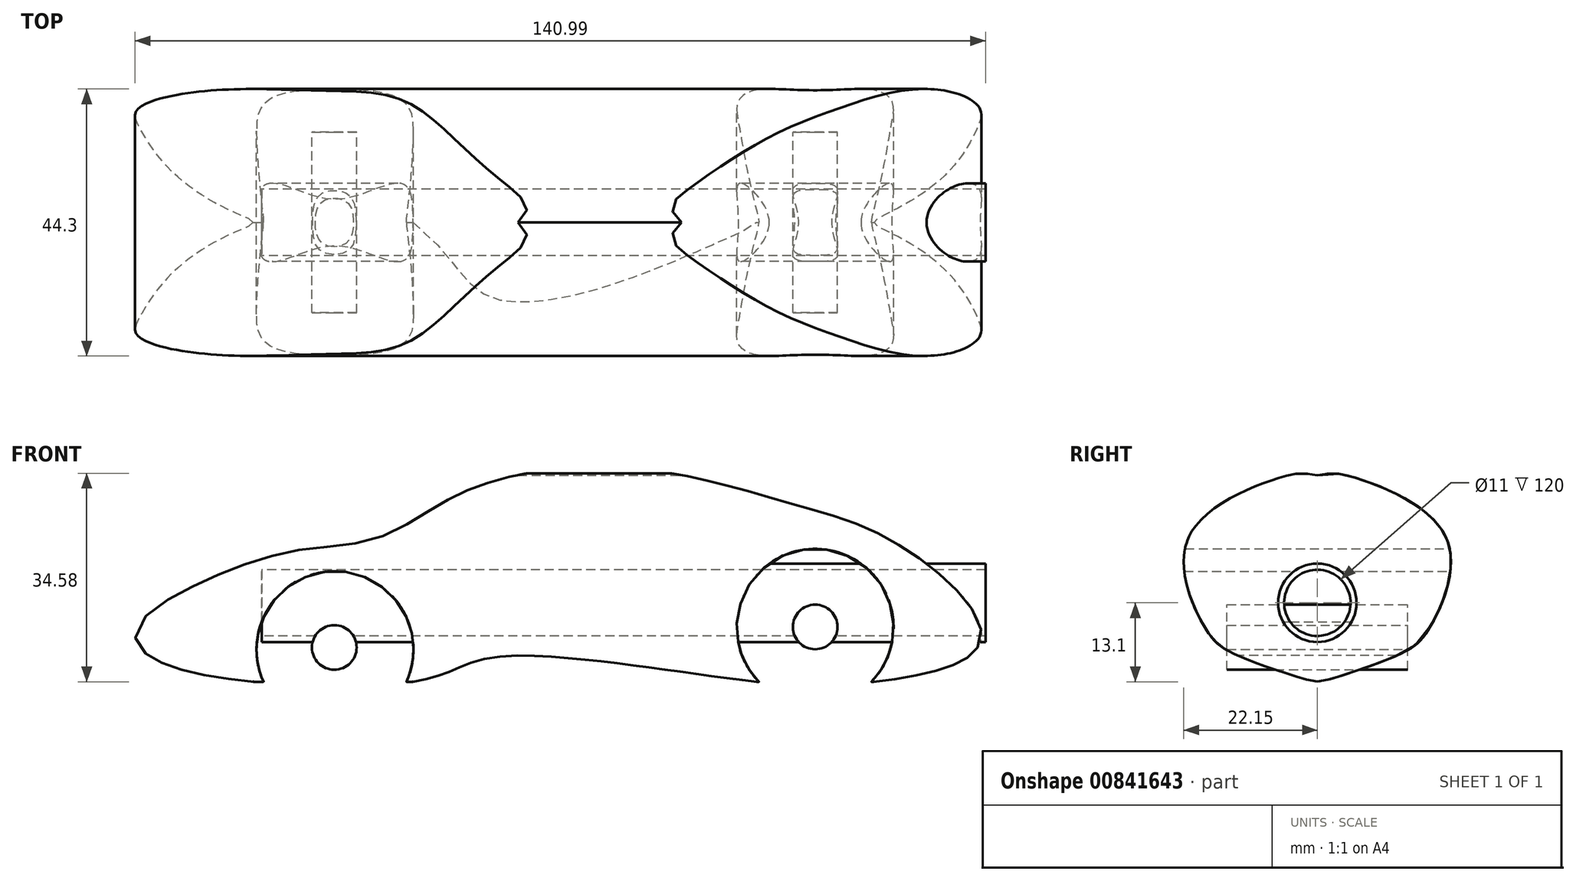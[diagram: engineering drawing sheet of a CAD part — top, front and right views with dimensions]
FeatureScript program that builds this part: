
annotation { "Feature Type Name" : "Feature", "Feature Type Description" : "" }
export const myFeature = defineFeature(function(context is Context, id is Id, definition is map)
    precondition{}
    {
        {
            var Q0;
            Q0=qCreatedBy(makeId("Front.planeOp"),FACE);
            var sketch = newSketch(context, id + "F0", { "sketchPlane" : qUnion([Q0])});
            skFitSpline(sketch, "E0", {"points": [v(-59.64, -4.2) * mm, v(-80.93, 4.21) * mm, v(-71.03, 11.94) * mm, v(-54.11, 17.74) * mm, v(-40.35, 19.91) * mm, v(-26.58, 27.4) * mm, v(-6.04, 31.51) * mm, v(11.6, 29.82) * mm, v(28.75, 25.23) * mm, v(44.36, 19.4) * mm, v(58.84, 6) * mm, v(41.05, -4.1) * mm], "startDerivative": vector(-453.54, 31.44) * mm, "endDerivative": vector(-506.77, -53.77) * mm});
            skArc(sketch, "E1", {"start": v(-36.05, -4.2) * mm, "mid": v(-47.84, 14.28) * mm, "end": v(-59.64, -4.2) * mm});
            skArc(sketch, "E2", {"start": v(41.05, -4.1) * mm, "mid": v(31.77, 18) * mm, "end": v(22.48, -4.1) * mm});
            skFitSpline(sketch, "E3", {"points": [v(-36.05, -4.2) * mm, v(-21.55, 0) * mm, v(22.48, -4.1) * mm], "startDerivative": vector(59.58, 6.01) * mm, "endDerivative": vector(57.48, -5.89) * mm});
            skLineSegment(sketch, "E4", {"start": v(-36.05, -4.2) * mm, "end": v(22.48, -4.1) * mm});
            skSolve(sketch);
        }
        {
            var Q0;
            Q0=makeQuery(id+"F0.imprint","IMPRINT",FACE,{"disambiguationData":[TD([[makeQuery(id+"F0.imprint","IMPRINT",EDGE,{"derivedFrom":sQuery(id+"F0.wireOp",EDGE,"E0")}),-1.0]])]});
            extrude(context, id + "F1", {"entities" : qUnion([Q0]), "endBound" : BoundingType.SYMMETRIC, "depth" : 45 * mm, "offsetDistance" : 25 * mm});
        }
        {
            var Q0;
            Q0=qCreatedBy(makeId("Right.planeOp"),FACE);
            var sketch = newSketch(context, id + "F2", { "sketchPlane" : qUnion([Q0])});
            skFitSpline(sketch, "E5", {"points": [v(0, 30.22) * mm, v(3.28, 30.45) * mm, v(6.23, 29.8) * mm, v(21.23, 20.11) * mm, v(18.59, 4.84) * mm, v(12.58, 0) * mm, v(0, -4.05) * mm, v(0, -3.93) * mm], "startDerivative": vector(56.54, 11.22) * mm, "endDerivative": vector(3.77, 8.29) * mm});
            skFitSpline(sketch, "E6.MirrorCS", {"points": [v(0, 30.22) * mm, v(-3.28, 30.45) * mm, v(-6.23, 29.8) * mm, v(-21.23, 20.11) * mm, v(-18.59, 4.84) * mm, v(-12.58, 0) * mm, v(0, -4.05) * mm, v(0, -3.93) * mm], "startDerivative": vector(-56.54, 11.22) * mm, "endDerivative": vector(-3.77, 8.29) * mm});
            skLineSegment(sketch, "E7.bottom", {"start": v(36.38, 39.95) * mm, "end": v(-33.23, 39.95) * mm});
            skLineSegment(sketch, "E7.top", {"start": v(36.38, -10.43) * mm, "end": v(-33.23, -10.43) * mm});
            skLineSegment(sketch, "E7.left", {"start": v(36.38, 39.95) * mm, "end": v(36.38, -10.43) * mm});
            skLineSegment(sketch, "E7.right", {"start": v(-33.23, 39.95) * mm, "end": v(-33.23, -10.43) * mm});
            skSolve(sketch);
        }
        {
            var Q0;
            Q0=makeQuery(id+"F2.imprint","IMPRINT",FACE,{"disambiguationData":[TD([[makeQuery(id+"F2.imprint","IMPRINT",EDGE,{"derivedFrom":sQuery(id+"F2.wireOp",EDGE,"E7.bottom")}),1.0]])]});
            extrude(context, id + "F3", {"entities" : qUnion([Q0]), "operationType" : NewBodyOperationType.REMOVE, "endBound" : BoundingType.SYMMETRIC, "oppositeDirection" : true, "depth" : 170 * mm, "offsetDistance" : 25 * mm});
        }
        {
            var Q0;
            Q0=makeQuery(id+"F2.imprint","IMPRINT",FACE,{"disambiguationData":[TD([[makeQuery(id+"F2.imprint","IMPRINT",EDGE,{"derivedFrom":sQuery(id+"F2.wireOp",EDGE,"E7.bottom")}),1.0]])]});
            var sketch = newSketch(context, id + "F4", { "sketchPlane" : qUnion([Q0])});
            skCircle(sketch, "E8", {"center": v(0, 9.03) * mm, "radius": 6.5 * mm});
            skCircle(sketch, "E9", {"center": v(0, 9.03) * mm, "radius": 5.5 * mm});
            skSolve(sketch);
        }
        {
            var Q0;
            Q0=makeQuery(id+"F4.imprint","IMPRINT",FACE,{"disambiguationData":[TD([[makeQuery(id+"F4.imprint","IMPRINT",EDGE,{"derivedFrom":sQuery(id+"F4.wireOp",EDGE,"E9")}),1.0]])]});
            var Q1;
            Q1=sQuery(id+"F4.wireOp",EDGE,"E8");
            extrude(context, id + "F5", {"entities" : qUnion([Q0]), "operationType" : NewBodyOperationType.REMOVE, "surfaceEntities" : qUnion([Q1]), "depth" : 60 * mm, "offsetDistance" : 25 * mm, "hasSecondDirection" : true, "secondDirectionOppositeDirection" : true, "secondDirectionDepth" : 60 * mm});
        }
        {
            var Q0;
            Q0=makeQuery(id+"F4.imprint","IMPRINT",FACE,{"disambiguationData":[TD([[makeQuery(id+"F4.imprint","IMPRINT",EDGE,{"derivedFrom":sQuery(id+"F4.wireOp",EDGE,"E8")}),1.0]])]});
            extrude(context, id + "F6", {"entities" : qUnion([Q0]), "operationType" : NewBodyOperationType.ADD, "depth" : 60 * mm, "offsetDistance" : 25 * mm, "hasSecondDirection" : true, "secondDirectionOppositeDirection" : true, "secondDirectionDepth" : 60 * mm});
        }
        {
            var Q0;
            Q0=qCreatedBy(makeId("Front.planeOp"),FACE);
            var sketch = newSketch(context, id + "F7", { "sketchPlane" : qUnion([Q0])});
            skCircle(sketch, "E10", {"center": v(-47.95, 1.63) * mm, "radius": 3.7 * mm});
            skSolve(sketch);
        }
        {
            var Q0;
            Q0=makeQuery(id+"F7.imprint","IMPRINT",FACE,{"disambiguationData":[TD([[makeQuery(id+"F7.imprint","IMPRINT",EDGE,{"derivedFrom":sQuery(id+"F7.wireOp",EDGE,"E10")}),1.0]])]});
            extrude(context, id + "F8", {"entities" : qUnion([Q0]), "operationType" : NewBodyOperationType.ADD, "depth" : 15 * mm, "offsetDistance" : 25 * mm, "hasSecondDirection" : true, "secondDirectionOppositeDirection" : true, "secondDirectionDepth" : 15 * mm});
        }
        {
            var Q0;
            Q0=qCreatedBy(makeId("Front.planeOp"),FACE);
            var sketch = newSketch(context, id + "F9", { "sketchPlane" : qUnion([Q0])});
            skCircle(sketch, "E11", {"center": v(31.77, 5.02) * mm, "radius": 3.7 * mm});
            skSolve(sketch);
        }
        {
            var Q0;
            Q0=makeQuery(id+"F9.imprint","IMPRINT",FACE,{"disambiguationData":[TD([[makeQuery(id+"F9.imprint","IMPRINT",EDGE,{"derivedFrom":sQuery(id+"F9.wireOp",EDGE,"E11")}),1.0]])]});
            extrude(context, id + "F10", {"entities" : qUnion([Q0]), "operationType" : NewBodyOperationType.ADD, "depth" : 15 * mm, "offsetDistance" : 25 * mm, "hasSecondDirection" : true, "secondDirectionOppositeDirection" : true, "secondDirectionDepth" : 15 * mm});
        }
    });
